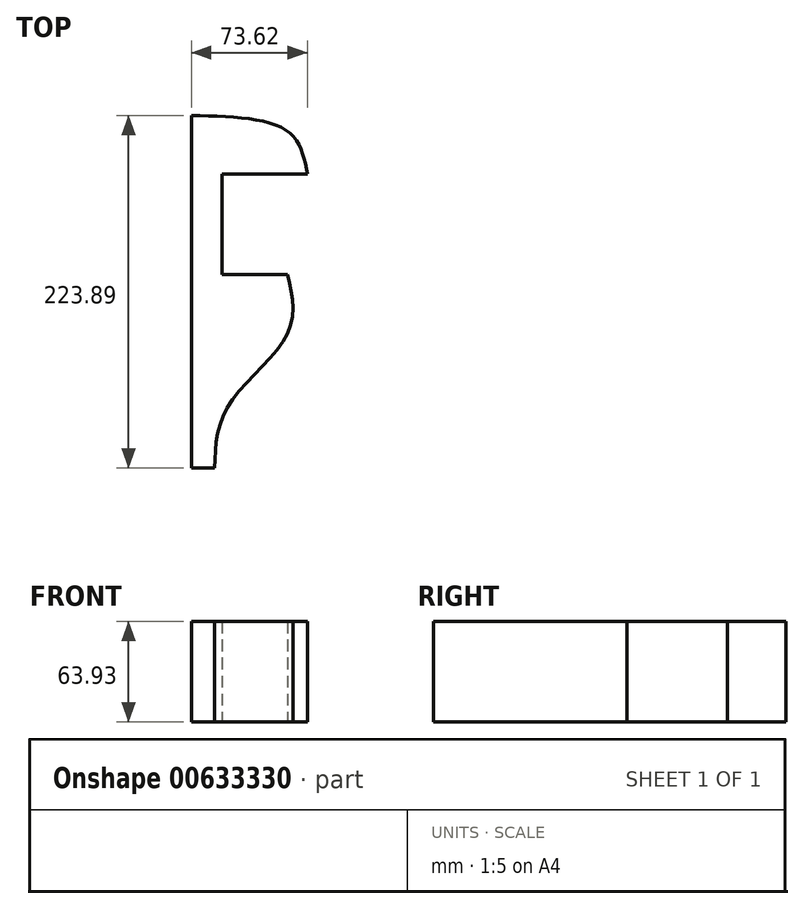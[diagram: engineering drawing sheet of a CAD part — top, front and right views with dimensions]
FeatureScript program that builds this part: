
annotation { "Feature Type Name" : "Feature", "Feature Type Description" : "" }
export const myFeature = defineFeature(function(context is Context, id is Id, definition is map)
    precondition{}
    {
        {
            var Q0;
            Q0=qCreatedBy(makeId("Top.planeOp"),FACE);
            var sketch = newSketch(context, id + "F0", { "sketchPlane" : qUnion([Q0])});
            skFitSpline(sketch, "E0", {"points": [v(0, 125) * mm, v(61.5, 114.6) * mm, v(73.62, 87.75) * mm], "startDerivative": vector(125.69, -3.2) * mm, "endDerivative": vector(14.7, -75.77) * mm});
            skLineSegment(sketch, "E1", {"start": v(73.62, 87.75) * mm, "end": v(19.49, 87.75) * mm});
            skLineSegment(sketch, "E2", {"start": v(19.49, 87.75) * mm, "end": v(19.49, 24.1) * mm});
            skLineSegment(sketch, "E3", {"start": v(19.49, 24.1) * mm, "end": v(61.06, 24.1) * mm});
            skFitSpline(sketch, "E4", {"points": [v(61.06, 24.1) * mm, v(61.06, -13.15) * mm, v(23.39, -59.5) * mm, v(14.72, -98.9) * mm], "startDerivative": vector(28.16, -123.96) * mm, "endDerivative": vector(-3.49, -126.39) * mm});
            skLineSegment(sketch, "E5", {"start": v(14.72, -98.9) * mm, "end": v(0, -98.9) * mm});
            skLineSegment(sketch, "E6", {"start": v(0, -98.9) * mm, "end": v(0, 125) * mm});
            skSolve(sketch);
        }
        {
            var Q0;
            Q0=makeQuery(id+"F0.imprint","IMPRINT",FACE,{"disambiguationData":[TD([[makeQuery(id+"F0.imprint","IMPRINT",EDGE,{"derivedFrom":sQuery(id+"F0.wireOp",EDGE,"E0")}),-1.0]])]});
            extrude(context, id + "F1", {"entities" : qUnion([Q0]), "depth" : 63.93 * mm, "offsetDistance" : 25.4 * mm});
        }
    });
